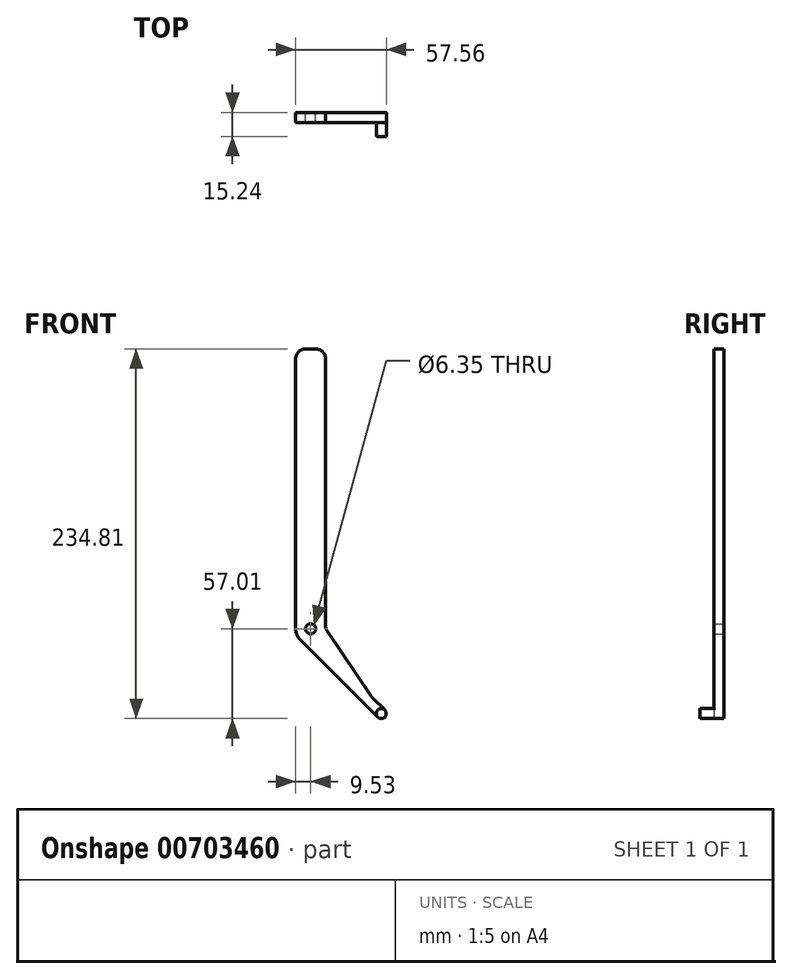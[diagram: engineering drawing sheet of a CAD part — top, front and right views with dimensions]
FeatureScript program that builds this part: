
annotation { "Feature Type Name" : "Feature", "Feature Type Description" : "" }
export const myFeature = defineFeature(function(context is Context, id is Id, definition is map)
    precondition{}
    {
        {
            var Q0;
            Q0=qCreatedBy(makeId("Front.planeOp"),FACE);
            var sketch = newSketch(context, id + "F0", { "sketchPlane" : qUnion([Q0])});
            skCircle(sketch, "E0", {"center": v(0, 0) * mm, "radius": 3.18 * mm});
            skArc(sketch, "E1", {"start": v(6.74, 6.74) * mm, "mid": v(-6.74, 6.74) * mm, "end": v(-6.74, -6.74) * mm});
            skLineSegment(sketch, "E2", {"start": v(-9.53, 0) * mm, "end": v(-9.53, 171.45) * mm});
            skLineSegment(sketch, "E3", {"start": v(9.53, 1.94) * mm, "end": v(9.53, 171.45) * mm});
            skLineSegment(sketch, "E4", {"start": v(-3.17, 177.8) * mm, "end": v(3.17, 177.8) * mm});
            skPoint(sketch, "E5.visualSharp", {"position": v(9.53, 177.8) * mm});
            skArc(sketch, "E5.filletArc", {"start": v(9.53, 171.45) * mm, "mid": v(7.67, 175.94) * mm, "end": v(3.18, 177.8) * mm});
            skPoint(sketch, "E6.visualSharp", {"position": v(-9.53, 177.8) * mm});
            skArc(sketch, "E6.filletArc", {"start": v(-3.17, 177.8) * mm, "mid": v(-7.67, 175.94) * mm, "end": v(-9.53, 171.45) * mm});
            skLineSegment(sketch, "E7", {"start": v(2.25, 2.25) * mm, "end": v(6.74, 6.74) * mm});
            skLineSegment(sketch, "E8", {"start": v(-2.25, -2.25) * mm, "end": v(-6.74, -6.74) * mm});
            skLineSegment(sketch, "E9", {"start": v(-6.74, -6.74) * mm, "end": v(42.6, -56.08) * mm});
            skLineSegment(sketch, "E10.0", {"start": v(39.04, -43.53) * mm, "end": v(47.1, -51.59) * mm});
            skArc(sketch, "E11", {"start": v(42.6, -56.08) * mm, "mid": v(47.1, -56.08) * mm, "end": v(47.1, -51.59) * mm});
            skLineSegment(sketch, "E12", {"start": v(10.61, -1.6) * mm, "end": v(38.27, -42.6) * mm});
            skArc(sketch, "E13.filletArc", {"start": v(38.27, -42.6) * mm, "mid": v(38.63, -43.08) * mm, "end": v(39.04, -43.53) * mm});
            skPoint(sketch, "E14.visualSharp", {"position": v(9.53, 0) * mm});
            skArc(sketch, "E14.filletArc", {"start": v(9.52, 1.94) * mm, "mid": v(9.8, 0.08) * mm, "end": v(10.61, -1.6) * mm});
            skSolve(sketch);
        }
        {
            var Q0;
            Q0 = qSketchRegion(id + "F0", true);
            extrude(context, id + "F1", {"entities" : qUnion([Q0]), "depth" : 6.35 * mm, "offsetDistance" : 25.4 * mm});
        }
        {
            var Q0;
            Q0=makeQuery(id+"F1.opExtrude","CAP_FACE",FACE,{"disambiguationData":[OSD([sQuery(id+"F0.wireOp",EDGE,"E0"),sQuery(id+"F0.wireOp",EDGE,"E1"),sQuery(id+"F0.wireOp",EDGE,"E2"),sQuery(id+"F0.wireOp",EDGE,"E3"),sQuery(id+"F0.wireOp",EDGE,"E4"),sQuery(id+"F0.wireOp",EDGE,"E5.filletArc"),sQuery(id+"F0.wireOp",EDGE,"E6.filletArc"),sQuery(id+"F0.wireOp",EDGE,"E9"),sQuery(id+"F0.wireOp",EDGE,"E10.0"),sQuery(id+"F0.wireOp",EDGE,"C7YqjFQK-a11p-aZnH-W3Ji-PaBIqbtFGTE1"),sQuery(id+"F0.wireOp",EDGE,"E11")])],"isStart":false});
            var sketch = newSketch(context, id + "F2", { "sketchPlane" : qUnion([Q0])});
            skCircle(sketch, "E15", {"center": v(44.85, -53.83) * mm, "radius": 3.18 * mm});
            skSolve(sketch);
        }
        {
            var Q0;
            Q0 = qSketchRegion(id + "F2", true);
            extrude(context, id + "F3", {"entities" : qUnion([Q0]), "operationType" : NewBodyOperationType.ADD, "depth" : 8.9 * mm, "offsetDistance" : 25.4 * mm});
        }
    });
